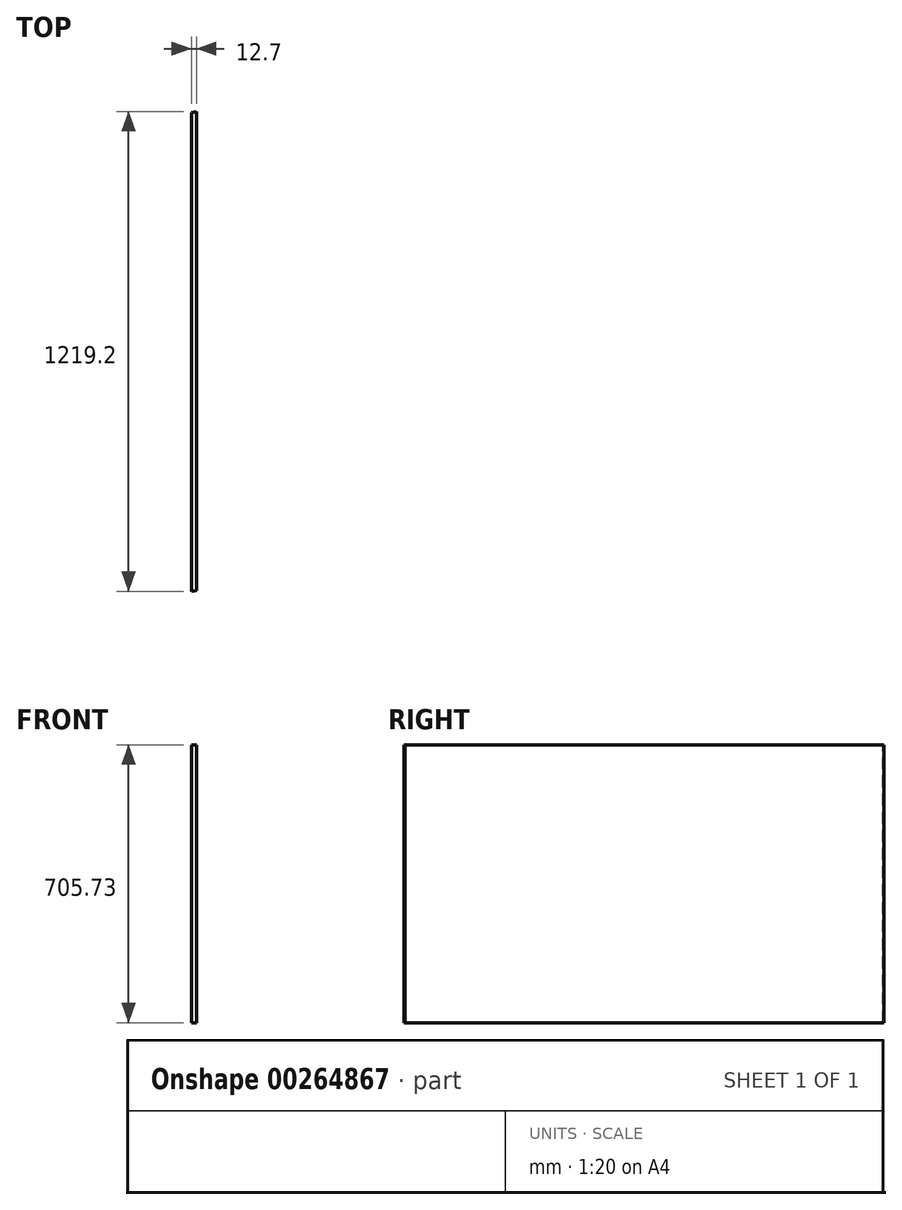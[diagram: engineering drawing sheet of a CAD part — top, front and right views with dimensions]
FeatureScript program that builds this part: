
annotation { "Feature Type Name" : "Feature", "Feature Type Description" : "" }
export const myFeature = defineFeature(function(context is Context, id is Id, definition is map)
    precondition{}
    {
        {
            var Q0;
            Q0=qCreatedBy(makeId("Right.planeOp"),FACE);
            var sketch = newSketch(context, id + "F0", { "sketchPlane" : qUnion([Q0])});
            skLineSegment(sketch, "E0.bottom", {"start": v(-741.28, 359.5) * mm, "end": v(477.92, 359.5) * mm});
            skLineSegment(sketch, "E0.top", {"start": v(-741.28, -346.22) * mm, "end": v(477.92, -346.22) * mm});
            skLineSegment(sketch, "E0.left", {"start": v(-741.28, 359.5) * mm, "end": v(-741.28, -346.22) * mm});
            skLineSegment(sketch, "E0.right", {"start": v(477.92, 359.5) * mm, "end": v(477.92, -346.22) * mm});
            skSolve(sketch);
        }
        {
            var Q0;
            Q0=makeQuery(id+"F0.imprint","IMPRINT",FACE,{"disambiguationData":[TD([[makeQuery(id+"F0.imprint","IMPRINT",EDGE,{"derivedFrom":sQuery(id+"F0.wireOp",EDGE,"E0.bottom")}),-1.0]])]});
            extrude(context, id + "F1", {"entities" : qUnion([Q0]), "depth" : 12.7 * mm});
        }
        {
            var Q0;
            Q0=makeQuery(id+"F1.opExtrude","SWEPT_FACE",FACE,{"disambiguationData":[OSD([sQuery(id+"F0.wireOp",EDGE,"E0.bottom")])]});
            var sketch = newSketch(context, id + "F2", { "sketchPlane" : qUnion([Q0])});
            skLineSegment(sketch, "E1", {"start": v(0, -741.28) * mm, "end": v(12.7, -738.54) * mm});
            skLineSegment(sketch, "E2", {"start": v(12.7, 477.92) * mm, "end": v(-24, 470.03) * mm});
            skLineSegment(sketch, "E3", {"start": v(-24, 470.03) * mm, "end": v(-24, 477.92) * mm});
            skLineSegment(sketch, "E4", {"start": v(-24, 477.92) * mm, "end": v(12.7, 477.92) * mm});
            skSolve(sketch);
        }
        {
            var Q0;
            {var subQ0=sQuery(id+"F2.wireOp",EDGE,"E1");Q0=makeQuery(id+"F2.imprint","IMPRINT",FACE,{"disambiguationData":[TD([[makeQuery(id+"F2.imprint","IMPRINT",EDGE,{"derivedFrom":subQ0}),-1.0]])]});}
            var Q1;
            {var subQ0=sQuery(id+"F2.wireOp",EDGE,"E3");Q1=makeQuery(id+"F2.imprint","IMPRINT",FACE,{"disambiguationData":[TD([[makeQuery(id+"F2.imprint","IMPRINT",EDGE,{"derivedFrom":subQ0}),-1.0]])]});}
            var Q2;
            {var subQ0=sQuery(id+"F2.wireOp",EDGE,"E4");var subQ2=sQuery(id+"F0.wireOp",EDGE,"E0.bottom");var subQ4=makeQuery(id+"F1.opExtrude","CAP_EDGE",EDGE,{"disambiguationData":[OSD([subQ2])],"isStart":true});var subQ6=makeQuery(id+"F2.imprint","INTERSECT",VERTEX,{"derivedFrom":[subQ4,subQ0]});Q2=makeQuery(id+"F2.imprint","IMPRINT",FACE,{"disambiguationData":[TD([[makeQuery(id+"F2.imprint","IMPRINT",EDGE,{"disambiguationData":[TD([[subQ6,1.0]])],"derivedFrom":subQ4}),-1.0]])]});}
            extrude(context, id + "F3", {"entities" : qUnion([Q0, Q1, Q2]), "operationType" : NewBodyOperationType.REMOVE, "endBound" : BoundingType.THROUGH_ALL, "oppositeDirection" : true, "depth" : 25.4 * mm, "offsetDistance" : 25.4 * mm});
        }
    });
